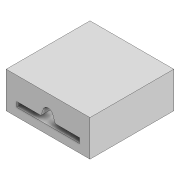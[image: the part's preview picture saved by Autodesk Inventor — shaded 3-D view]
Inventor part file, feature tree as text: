
AUTODESK INVENTOR PART (.ipt)
format: ipt  version: 2022 (Build 260153000, 153)  size: 100,864 bytes
history: native  units: mm
features: extrude x1, sketch x1
ambient origin geometry x8: Origin, YZ Plane, XZ Plane, XY Plane, X Axis, Y Axis, Z Axis, Center Point
bodies: Solid1 (feature_tree)
feature tree (2):
  extrude  "Extrusion1"  Depth=7.5mm
  sketch  "Sketch1"  dims[d0=10.0mm d1=7.5mm d2=3.75mm d3=5.0mm d4=1.0mm d5=0.6mm d6=1.2mm d7=1.5mm d8=12.217305mm d9=12.217305mm d10=10.0mm d11=0.0mm]
